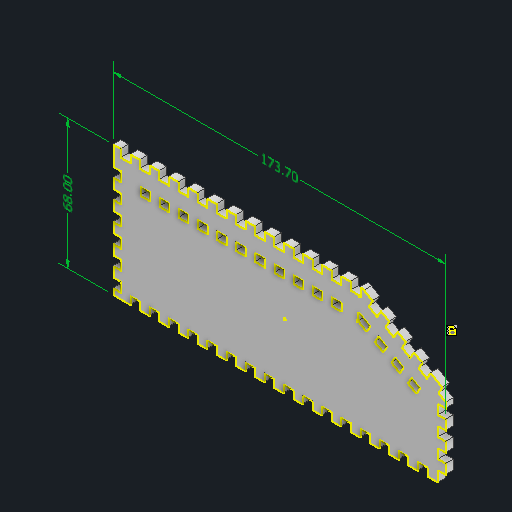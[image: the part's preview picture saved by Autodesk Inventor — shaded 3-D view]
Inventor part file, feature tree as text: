
AUTODESK INVENTOR PART (.ipt)
format: ipt  version: 2023 (Build 270158030, 158C)  size: 1,044,480 bytes
history: native  units: mm
features: extrude x5, sketch x5, other x3, direct_edit x3, move_body x3, delete_face x1, projected_geometry x1
ambient origin geometry x8: Origin, YZ Plane, XZ Plane, XY Plane, X Axis, Y Axis, Z Axis, Center Point
bodies: Solid1 (feature_tree)
feature tree (21):
  other  "Annotations"
  extrude  "Extrusion1"  Depth=60.0mm
  sketch  "Sketch2"  dims[d2=47.0mm d3=30.0deg]
  extrude  "Extrusion2"  TaperAngle=30.0deg  [1 undecoded]
  extrude  "Extrusion3"  Depth=4.0mm TaperAngle=0.0deg
  extrude  "Extrusion4"  Depth=4.0mm
  extrude  "Extrusion5"  Depth=5.0mm
  direct_edit  "Direct Edit1"
  delete_face  "Delete Face1"
  direct_edit  "Direct Edit2"
  direct_edit  "Direct Edit3"
  sketch  "Sketch7"  dims[d9=120.0mm d11=10.0mm d12=10.0mm d14=10.0mm d16=5.0mm d17=4.0mm d18=50.0mm d20=10.0mm d21=10.0mm d23=10.0mm d25=7.0mm d26=5.0mm d27=4.0mm d28=120.0mm d30=10.0mm d31=10.0mm d33=10.0mm d35=5.0mm d36=30.0deg d37=4.0mm d38=40.0mm d40=10.0mm d41=10.0mm d43=10.0mm d45=5.0mm d46=4.0mm d47=170.0mm d49=10.0mm d50=10.0mm d52=10.0mm d54=4.0mm d55=0.0mm d56=4.0mm d57=0.0mm d58=4.0mm d59=10.0mm d60=4.0mm d61=5.0mm d62=60.0mm d64=10.0mm d65=10.0mm d67=10.0mm d69=4.0mm d70=0.0mm d71=5.0mm d72=5.0mm d73=4.0mm d74=4.0mm d75=5.0mm d76=30.0mm d78=10.0mm d79=10.0mm d81=10.0mm d83=4.0mm d84=0.0mm d91=-9.75mm d92=0.0mm d93=16.75mm d94=-1.25mm d95=0.0mm d96=0.0mm d97=-3.75mm d98=0.0mm d99=0.0mm d85=2.396448mm d86=5.019131mm d87=68.0mm d88=5.652543mm d89=4.315711mm d90=173.703194mm]
  sketch  "Sketch1"  dims[d0=172.0mm d1=60.0mm]
  sketch  "Sketch3"  dims[d4=125.0mm d5=4.0mm d6=0.0mm]
  sketch  "Sketch4"  dims[d7=5.0mm d8=4.0mm]
  projected_geometry  "Projected Loop3"
  move_body  "Move1"
  move_body  "Move2"
  move_body  "Move3"
  other  "Linear Dimension 1"
  other  "Linear Dimension 2"
note: 1 required parameter value undecoded (feature->parameter linkage not recoverable at this tier; creation-order binding heuristic only, values carry confidence <= 0.55)
